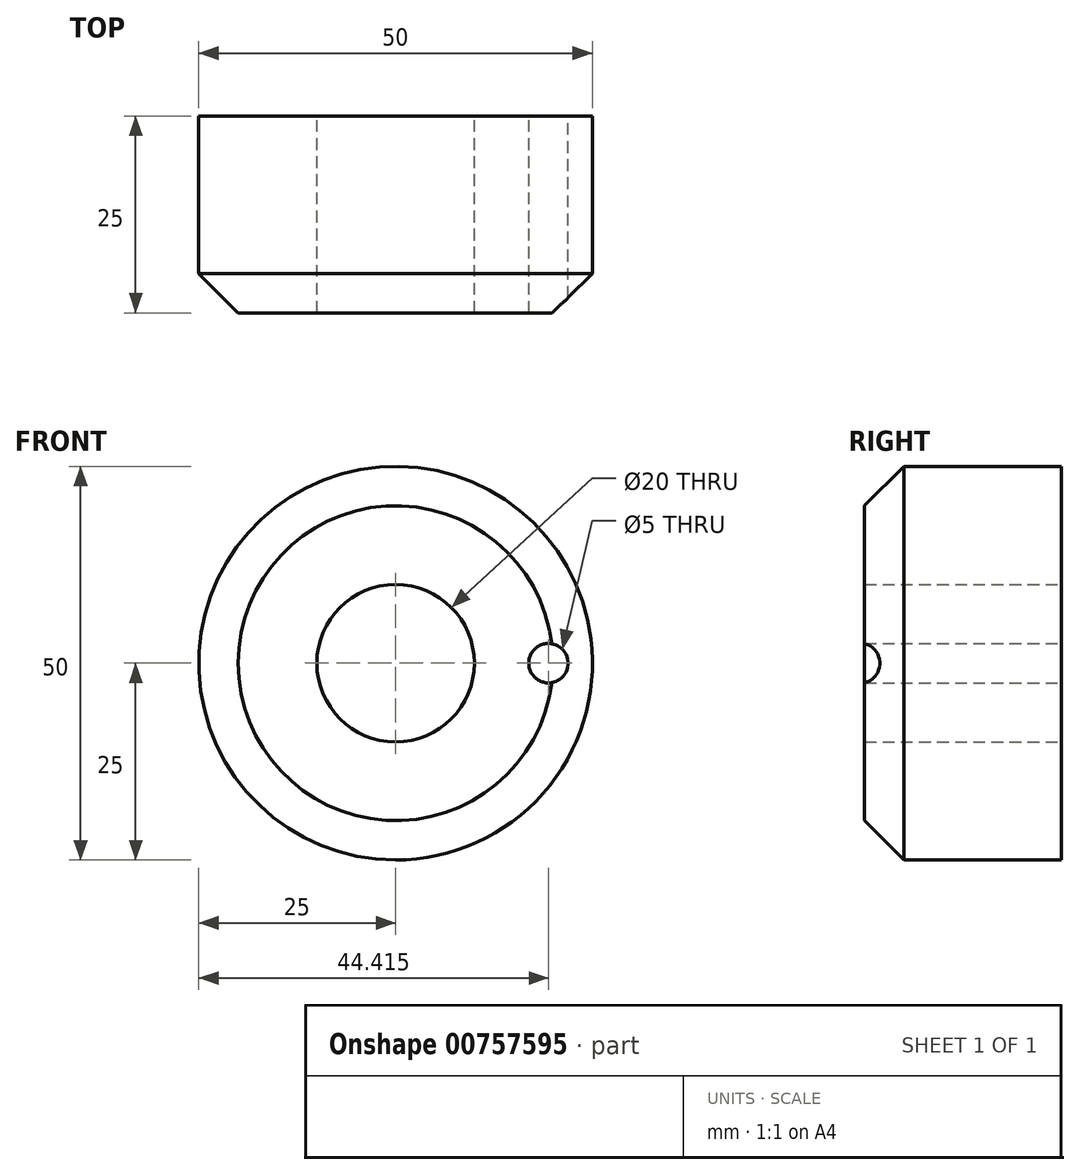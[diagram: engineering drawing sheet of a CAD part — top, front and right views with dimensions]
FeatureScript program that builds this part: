
annotation { "Feature Type Name" : "Feature", "Feature Type Description" : "" }
export const myFeature = defineFeature(function(context is Context, id is Id, definition is map)
    precondition{}
    {
        {
            var Q0;
            Q0=qCreatedBy(makeId("Front.planeOp"),FACE);
            var sketch = newSketch(context, id + "F0", { "sketchPlane" : qUnion([Q0])});
            skCircle(sketch, "E0", {"center": v(0, 0) * mm, "radius": 25 * mm});
            skSolve(sketch);
        }
        {
            var Q0;
            Q0=makeQuery(id+"F0.imprint","IMPRINT",FACE,{"disambiguationData":[TD([[makeQuery(id+"F0.imprint","IMPRINT",EDGE,{"derivedFrom":sQuery(id+"F0.wireOp",EDGE,"E0")}),1.0]])]});
            extrude(context, id + "F1", {"entities" : qUnion([Q0]), "depth" : 25 * mm, "offsetDistance" : 25 * mm});
        }
        {
            var Q0;
            Q0=qCreatedBy(makeId("Front.planeOp"),FACE);
            var sketch = newSketch(context, id + "F2", { "sketchPlane" : qUnion([Q0])});
            skCircle(sketch, "E1", {"center": v(0, 0) * mm, "radius": 10 * mm});
            skSolve(sketch);
        }
        {
            var Q0;
            Q0 = qSketchRegion(id + "F2", true);
            extrude(context, id + "F3", {"entities" : qUnion([Q0]), "operationType" : NewBodyOperationType.REMOVE, "depth" : 50 * mm, "offsetDistance" : 25 * mm});
        }
        {
            var Q0;
            Q0=makeQuery(id+"F1.opExtrude","CAP_EDGE",EDGE,{"disambiguationData":[OSD([sQuery(id+"F0.wireOp",EDGE,"E0")])],"isStart":false});
            chamfer(context, id + "F4", {"entities" : qUnion([Q0]), "width" : 5 * mm, "tangentPropagation" : true});
        }
        {
            var Q0;
            Q0=qCreatedBy(makeId("Front.planeOp"),FACE);
            var sketch = newSketch(context, id + "F5", { "sketchPlane" : qUnion([Q0])});
            skCircle(sketch, "E2", {"center": v(19.42, 0) * mm, "radius": 2.5 * mm});
            skSolve(sketch);
        }
        {
            var Q0;
            Q0=makeQuery(id+"F5.imprint","IMPRINT",FACE,{"disambiguationData":[TD([[makeQuery(id+"F5.imprint","IMPRINT",EDGE,{"derivedFrom":sQuery(id+"F5.wireOp",EDGE,"E2")}),1.0]])]});
            extrude(context, id + "F6", {"entities" : qUnion([Q0]), "operationType" : NewBodyOperationType.REMOVE, "depth" : 25 * mm, "offsetDistance" : 25 * mm});
        }
    });
